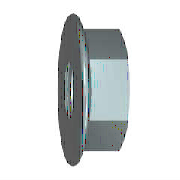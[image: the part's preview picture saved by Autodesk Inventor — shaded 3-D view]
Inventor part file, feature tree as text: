
AUTODESK INVENTOR PART (.ipt)
format: ipt  version: 2011 (Build 150229000, 229)  size: 198,656 bytes
history: native  units: mm (DEFAULTED — no unit token found)
features: other x2, chamfer x1, hole x1, plane x1
ambient origin geometry x7: Origin, YZ Plane, XZ Plane, X Axis, Y Axis, Z Axis, Center Point
bodies: Body (feature_tree)
feature tree (5):
  other  "Ring"
  chamfer  "Chamfer1"  Distance=11.8mm
  hole  "Thread"  [1 undecoded]
  other  "Work Axis1"
  plane  "Work Plane1"
note: 1 required parameter value undecoded (feature->parameter linkage not recoverable at this tier; creation-order binding heuristic only, values carry confidence <= 0.55)
